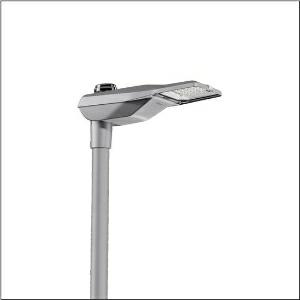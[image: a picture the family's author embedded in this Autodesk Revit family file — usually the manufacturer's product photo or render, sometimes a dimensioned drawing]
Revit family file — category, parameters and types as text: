
# Revit family: streetlight_sl_21_micro___st0_8a_5xe5c37n08cb_a39a
name_source: partatom
category: Lighting Fixtures
units: mm (PartAtom-declared; Revit-internal decimal feet)

## family parameters
Cut with Voids When Loaded = No
Host = Face
Light Source = No
Part Type = Normal
Room Calculation Point = No
Round Connector Dimension = Use Diameter
Shared = No

## types (1)
- --- (1 x LED, 2290 lm, 15.8 W, 3000K)
    Apparent Load = 16 VA
    CIE Flux Codes = 38 75 97 100 100
    Color Rendering = 70
    Color Temperature = 3000K
    Default Elevation = 1800 mm
    Description = Streetlight SL 21 micro, mast luminaire, primary light control with lens, of PMMA, primary optical cover: cover, of toughened safety glass, transparent, light distribution: ST0.8a, light emission: direct distribution, primary light characteristic: asymmetric, installation type: post-top, LED, 3G 1.5mm², High Power LED, rated luminous flux: 2.290lm, luminous efficacy: 145lm/W, light colour: 730, colour temperature: 3000K, control gear: NEMA (7pin), control: overheat protection, pre-setting: linear dimming characteristic, constant luminous flux control, time-dependent luminous flux control, flexible luminous flux parameterisation, mains connection: 230..240V, AC, 50/60Hz, connection cable pre-assembled, cable length: 6,5m, wiring characteristics: H07RN-F, start of lifetime: 16W, end of service life: 16W, reduction: 8W, luminaire housing, of diecast aluminium (EN AC-44300), powder-coated, Siteco® metallic grey (DB 702S), corrosivity category C5 mid according to DIN EN ISO 12944, multi-level sealing system, sealing non-destructively replaceable, inclination adjustable: 0°, 5°, 10°, 15°, length: 528mm, width: 235mm, height: 110mm, spigot size: 76/60mm (post-top), mounting height: 4..8m, protection rating (complete): IP66, insulation class (complete): insulation class I (protective earthing), certification: CE, ENEC, ENEC+, VDE, impact resistance: IK10, permissible operating ambient temperature for outdoor applications: -40..+50°C, standard-compliant lighting for roads and squares, packaging unit: 1 piece

Light Distribution: ST0.8a
    Height = 110 mm
    Lamp = 1 x LED
    Lamp Light Flux = 2290 lm
    Lamp Power = 15.8 W
    Lamp count = 1
    Length = 528 mm
    Luminous efficacy = 145 lm/W
    Manufacturer = Siteco
    ModVariant = No
    Model = 5XE5C37N08CB
    Number of Poles = 1
    OnlyDefault = Yes
    Power Factor = 1
    Product Name = Streetlight SL 21 micro | ST0.8a
    Product group = mast luminaire | pylon top
    ProductGroupID = 6100
    Protection Class = Protection class I
    Protection Degree = IP 66
    RLX_Detail_Level = 1
    RLX_Emergency_Light_Flux = 0 lm
    RLX_Emergency_Type = 0
    RLX_Emergency_Type_DB = No
    RlxData = <blob elided: 98225 chars, md5=a28a6994>
    Socket = socket
    Standby Power = 0 W
    System Light Flux = 2290 lm
    System Power = 16 W
    Type Comments = factory setting: luminous flux: 100 % | dim-lin: 254 | 300 mA
    Type Image = l_1294375.jpg
    URL = http://relux.com
    VarID = @adj_155891
    Voltage = 0 V
    Weight = 0.00 kg
    Width = 235 mm

## geometry (parser evidence)
native form markers: Blend x4, Sweep x10
no freeform markers — native parametric forms only
